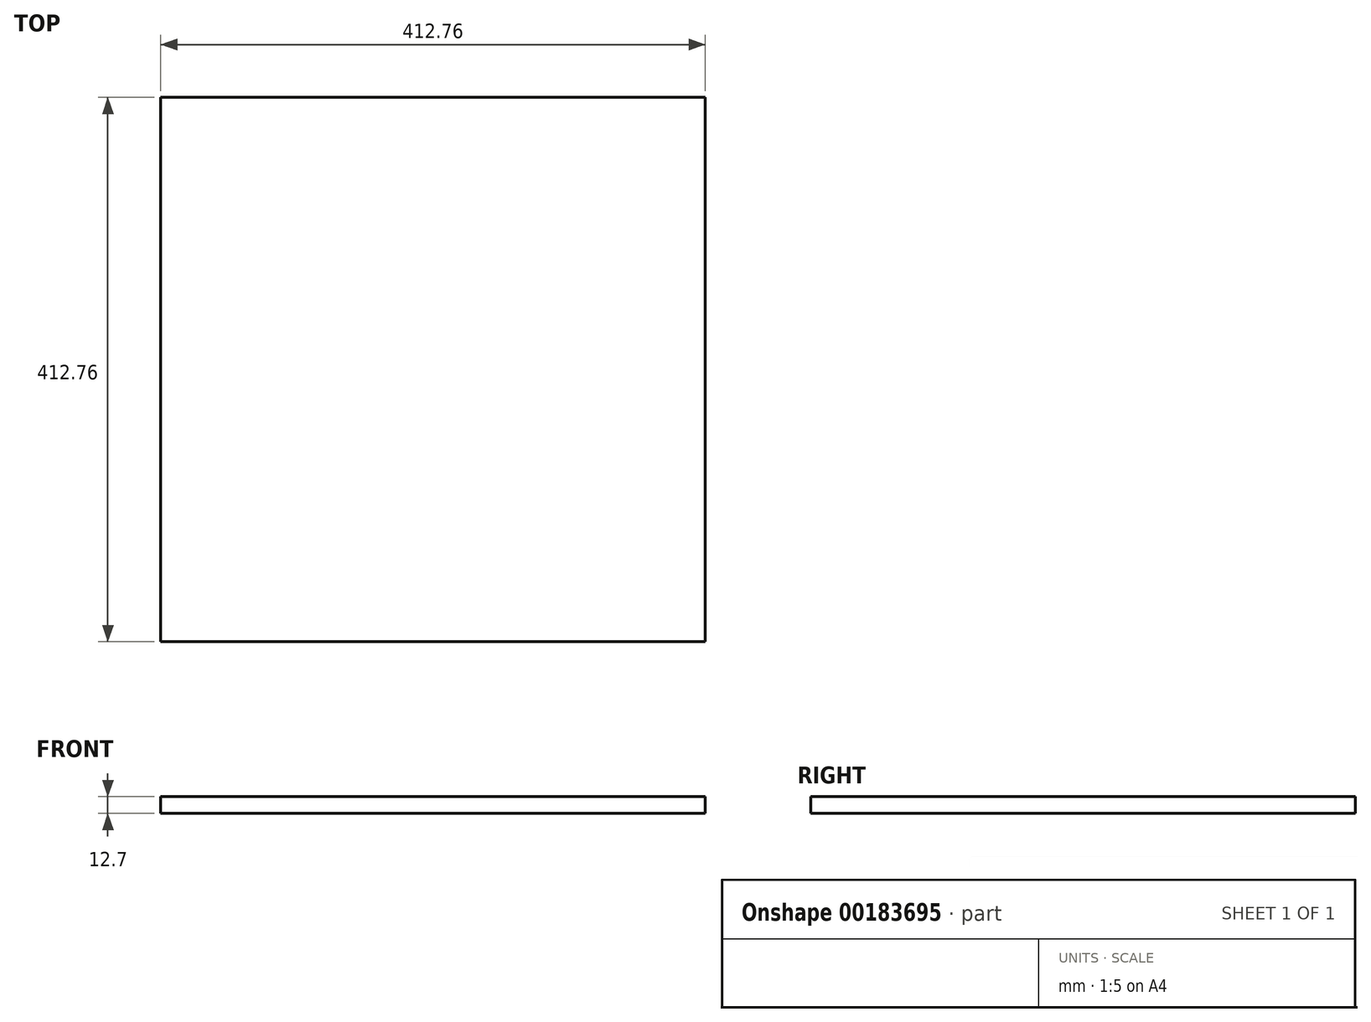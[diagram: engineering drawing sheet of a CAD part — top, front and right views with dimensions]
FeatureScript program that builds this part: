
annotation { "Feature Type Name" : "Feature", "Feature Type Description" : "" }
export const myFeature = defineFeature(function(context is Context, id is Id, definition is map)
    precondition{}
    {
        {
            var Q0;
            Q0=qCreatedBy(makeId("Front.planeOp"),FACE);
            var sketch = newSketch(context, id + "F0", { "sketchPlane" : qUnion([Q0])});
            skLineSegment(sketch, "E0.bottom", {"start": v(206.38, 6.35) * mm, "end": v(-206.38, 6.35) * mm});
            skLineSegment(sketch, "E0.top", {"start": v(206.38, -6.35) * mm, "end": v(-206.38, -6.35) * mm});
            skLineSegment(sketch, "E0.left", {"start": v(206.38, 6.35) * mm, "end": v(206.38, -6.35) * mm});
            skLineSegment(sketch, "E0.right", {"start": v(-206.38, 6.35) * mm, "end": v(-206.38, -6.35) * mm});
            skPoint(sketch, "E0.middle", {"position": v(0, 0) * mm});
            skSolve(sketch);
        }
        {
            var Q0;
            Q0=qSketchRegion(id+"F0",true);
            extrude(context, id + "F1", {"entities" : qUnion([Q0]), "endBound" : BoundingType.SYMMETRIC, "depth" : 412.75 * mm});
        }
    });
